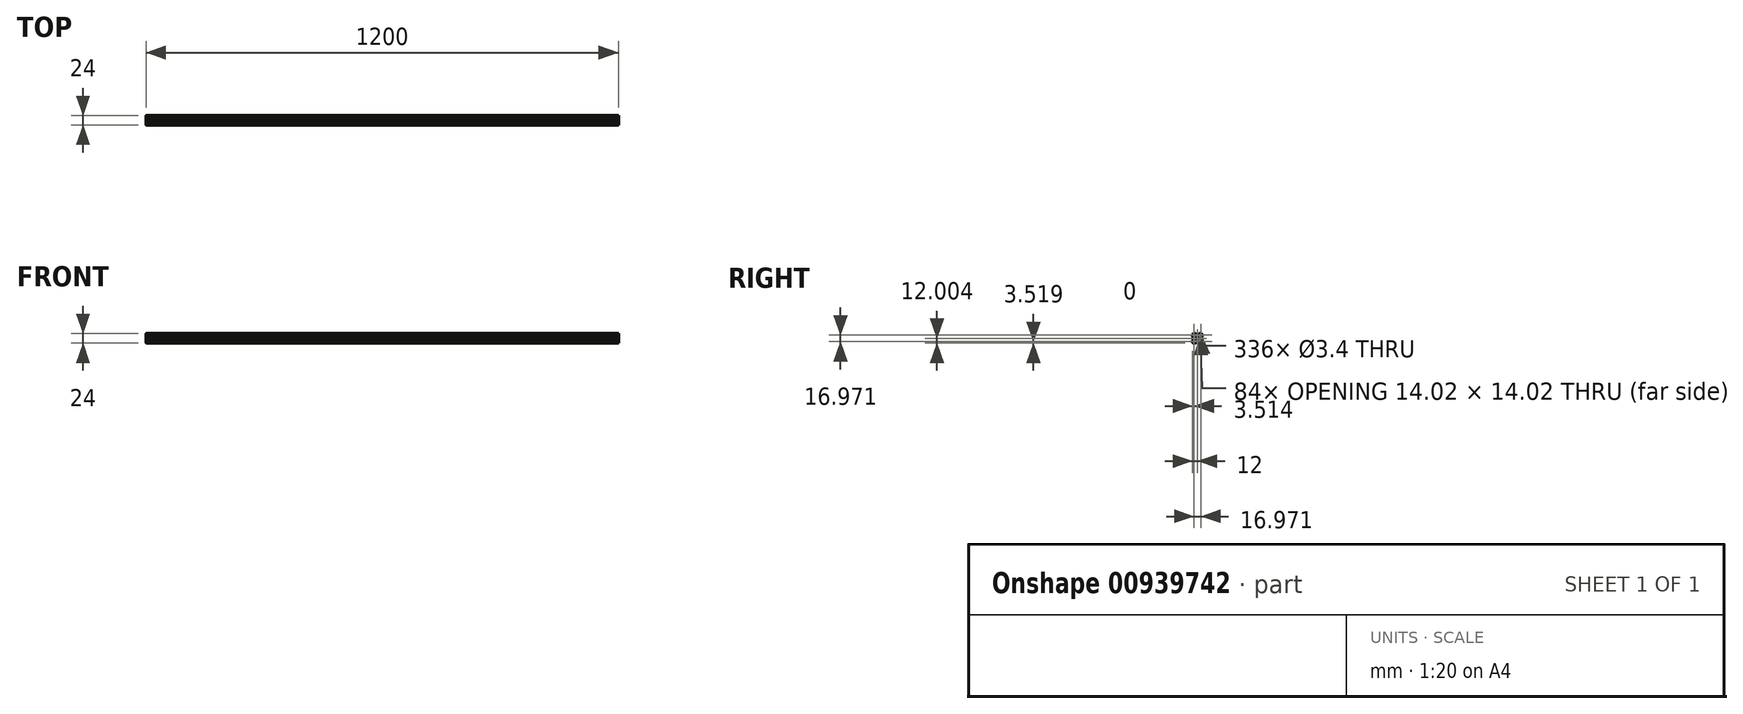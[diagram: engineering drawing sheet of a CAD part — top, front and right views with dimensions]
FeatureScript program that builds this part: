
annotation { "Feature Type Name" : "Feature", "Feature Type Description" : "" }
export const myFeature = defineFeature(function(context is Context, id is Id, definition is map)
    precondition{}
    {
        {
            var Q0;
            Q0=qCreatedBy(makeId("Right.planeOp"),FACE);
            var sketch = newSketch(context, id + "F0", { "sketchPlane" : qUnion([Q0])});
            skLineSegment(sketch, "E0.0.0", {"start": v(-5.44, -8.54) * mm, "end": v(5.56, -8.54) * mm});
            skLineSegment(sketch, "E0.0.1", {"start": v(5.56, -8.54) * mm, "end": v(5.56, -10.04) * mm});
            skLineSegment(sketch, "E0.0.2", {"start": v(5.56, -10.04) * mm, "end": v(4.06, -10.04) * mm});
            skLineSegment(sketch, "E0.0.3", {"start": v(4.06, -10.04) * mm, "end": v(4.06, -11.04) * mm});
            skLineSegment(sketch, "E0.0.4", {"start": v(4.06, -11.04) * mm, "end": v(5.06, -12.04) * mm});
            skLineSegment(sketch, "E0.0.5", {"start": v(5.06, -12.04) * mm, "end": v(8.04, -12.04) * mm});
            skLineSegment(sketch, "E0.0.6", {"start": v(8.04, -12.04) * mm, "end": v(8.54, -11.54) * mm});
            skLineSegment(sketch, "E0.0.7", {"start": v(8.54, -11.54) * mm, "end": v(9.04, -12.04) * mm});
            skLineSegment(sketch, "E0.0.8", {"start": v(9.04, -12.04) * mm, "end": v(10.57, -12.04) * mm});
            skArc(sketch, "E0.0.9", {"start": v(10.57, -12.04) * mm, "mid": v(11.34, -11.31) * mm, "end": v(12.06, -10.54) * mm});
            skLineSegment(sketch, "E0.0.10", {"start": v(12.06, -10.54) * mm, "end": v(12.06, -9.02) * mm});
            skLineSegment(sketch, "E0.0.11", {"start": v(12.06, -9.02) * mm, "end": v(11.56, -8.52) * mm});
            skLineSegment(sketch, "E0.0.12", {"start": v(11.56, -8.52) * mm, "end": v(12.06, -8.02) * mm});
            skLineSegment(sketch, "E0.0.13", {"start": v(12.06, -8.02) * mm, "end": v(12.06, -5.04) * mm});
            skLineSegment(sketch, "E0.0.14", {"start": v(12.06, -5.04) * mm, "end": v(11.06, -4.04) * mm});
            skLineSegment(sketch, "E0.0.15", {"start": v(11.06, -4.04) * mm, "end": v(10.06, -4.04) * mm});
            skLineSegment(sketch, "E0.0.16", {"start": v(10.06, -4.04) * mm, "end": v(10.06, -5.54) * mm});
            skLineSegment(sketch, "E0.0.17", {"start": v(10.06, -5.54) * mm, "end": v(8.56, -5.54) * mm});
            skLineSegment(sketch, "E0.0.18", {"start": v(8.56, -5.54) * mm, "end": v(8.56, 5.46) * mm});
            skLineSegment(sketch, "E0.0.19", {"start": v(8.56, 5.46) * mm, "end": v(10.06, 5.46) * mm});
            skLineSegment(sketch, "E0.0.20", {"start": v(10.06, 5.46) * mm, "end": v(10.06, 3.96) * mm});
            skLineSegment(sketch, "E0.0.21", {"start": v(10.06, 3.96) * mm, "end": v(11.06, 3.96) * mm});
            skLineSegment(sketch, "E0.0.22", {"start": v(11.06, 3.96) * mm, "end": v(12.06, 4.96) * mm});
            skLineSegment(sketch, "E0.0.23", {"start": v(12.06, 4.96) * mm, "end": v(12.06, 7.95) * mm});
            skLineSegment(sketch, "E0.0.24", {"start": v(12.06, 7.95) * mm, "end": v(11.56, 8.45) * mm});
            skLineSegment(sketch, "E0.0.25", {"start": v(11.56, 8.45) * mm, "end": v(12.06, 8.95) * mm});
            skLineSegment(sketch, "E0.0.26", {"start": v(12.06, 8.95) * mm, "end": v(12.06, 10.47) * mm});
            skArc(sketch, "E0.0.27", {"start": v(12.06, 10.47) * mm, "mid": v(11.34, 11.24) * mm, "end": v(10.57, 11.96) * mm});
            skLineSegment(sketch, "E0.0.28", {"start": v(10.57, 11.96) * mm, "end": v(9.04, 11.96) * mm});
            skLineSegment(sketch, "E0.0.29", {"start": v(9.04, 11.96) * mm, "end": v(8.54, 11.46) * mm});
            skLineSegment(sketch, "E0.0.30", {"start": v(8.54, 11.46) * mm, "end": v(8.04, 11.96) * mm});
            skLineSegment(sketch, "E0.0.31", {"start": v(8.04, 11.96) * mm, "end": v(5.06, 11.96) * mm});
            skLineSegment(sketch, "E0.0.32", {"start": v(5.06, 11.96) * mm, "end": v(4.06, 10.96) * mm});
            skLineSegment(sketch, "E0.0.33", {"start": v(4.06, 10.96) * mm, "end": v(4.06, 9.96) * mm});
            skLineSegment(sketch, "E0.0.34", {"start": v(4.06, 9.96) * mm, "end": v(5.56, 9.96) * mm});
            skLineSegment(sketch, "E0.0.35", {"start": v(5.56, 9.96) * mm, "end": v(5.56, 8.46) * mm});
            skLineSegment(sketch, "E0.0.36", {"start": v(5.56, 8.46) * mm, "end": v(-5.44, 8.46) * mm});
            skLineSegment(sketch, "E0.0.37", {"start": v(-5.44, 8.46) * mm, "end": v(-5.44, 9.96) * mm});
            skLineSegment(sketch, "E0.0.38", {"start": v(-5.44, 9.96) * mm, "end": v(-3.94, 9.96) * mm});
            skLineSegment(sketch, "E0.0.39", {"start": v(-3.94, 9.96) * mm, "end": v(-3.94, 10.96) * mm});
            skLineSegment(sketch, "E0.0.40", {"start": v(-3.94, 10.96) * mm, "end": v(-4.94, 11.96) * mm});
            skLineSegment(sketch, "E0.0.41", {"start": v(-4.94, 11.96) * mm, "end": v(-7.93, 11.96) * mm});
            skLineSegment(sketch, "E0.0.42", {"start": v(-7.93, 11.96) * mm, "end": v(-8.43, 11.46) * mm});
            skLineSegment(sketch, "E0.0.43", {"start": v(-8.43, 11.46) * mm, "end": v(-8.93, 11.96) * mm});
            skLineSegment(sketch, "E0.0.44", {"start": v(-8.93, 11.96) * mm, "end": v(-10.45, 11.96) * mm});
            skArc(sketch, "E0.0.45", {"start": v(-10.45, 11.96) * mm, "mid": v(-11.22, 11.24) * mm, "end": v(-11.94, 10.47) * mm});
            skLineSegment(sketch, "E0.0.46", {"start": v(-11.94, 10.47) * mm, "end": v(-11.94, 8.95) * mm});
            skLineSegment(sketch, "E0.0.47", {"start": v(-11.94, 8.95) * mm, "end": v(-11.44, 8.45) * mm});
            skLineSegment(sketch, "E0.0.48", {"start": v(-11.44, 8.45) * mm, "end": v(-11.94, 7.95) * mm});
            skLineSegment(sketch, "E0.0.49", {"start": v(-11.94, 7.95) * mm, "end": v(-11.94, 4.96) * mm});
            skLineSegment(sketch, "E0.0.50", {"start": v(-11.94, 4.96) * mm, "end": v(-10.94, 3.96) * mm});
            skLineSegment(sketch, "E0.0.51", {"start": v(-10.94, 3.96) * mm, "end": v(-9.94, 3.96) * mm});
            skLineSegment(sketch, "E0.0.52", {"start": v(-9.94, 3.96) * mm, "end": v(-9.94, 5.46) * mm});
            skLineSegment(sketch, "E0.0.53", {"start": v(-9.94, 5.46) * mm, "end": v(-8.44, 5.46) * mm});
            skLineSegment(sketch, "E0.0.54", {"start": v(-8.44, 5.46) * mm, "end": v(-8.44, -5.54) * mm});
            skLineSegment(sketch, "E0.0.55", {"start": v(-8.44, -5.54) * mm, "end": v(-9.94, -5.54) * mm});
            skLineSegment(sketch, "E0.0.56", {"start": v(-9.94, -5.54) * mm, "end": v(-9.94, -4.04) * mm});
            skLineSegment(sketch, "E0.0.57", {"start": v(-9.94, -4.04) * mm, "end": v(-10.94, -4.04) * mm});
            skLineSegment(sketch, "E0.0.58", {"start": v(-10.94, -4.04) * mm, "end": v(-11.94, -5.04) * mm});
            skLineSegment(sketch, "E0.0.59", {"start": v(-11.94, -5.04) * mm, "end": v(-11.94, -8.02) * mm});
            skLineSegment(sketch, "E0.0.60", {"start": v(-11.94, -8.02) * mm, "end": v(-11.44, -8.52) * mm});
            skLineSegment(sketch, "E0.0.61", {"start": v(-11.44, -8.52) * mm, "end": v(-11.94, -9.02) * mm});
            skLineSegment(sketch, "E0.0.62", {"start": v(-11.94, -9.02) * mm, "end": v(-11.94, -10.54) * mm});
            skArc(sketch, "E0.0.63", {"start": v(-11.94, -10.54) * mm, "mid": v(-11.22, -11.31) * mm, "end": v(-10.45, -12.04) * mm});
            skLineSegment(sketch, "E0.0.64", {"start": v(-10.45, -12.04) * mm, "end": v(-8.93, -12.04) * mm});
            skLineSegment(sketch, "E0.0.65", {"start": v(-8.93, -12.04) * mm, "end": v(-8.43, -11.54) * mm});
            skLineSegment(sketch, "E0.0.66", {"start": v(-8.43, -11.54) * mm, "end": v(-7.93, -12.04) * mm});
            skLineSegment(sketch, "E0.0.67", {"start": v(-7.93, -12.04) * mm, "end": v(-4.94, -12.04) * mm});
            skLineSegment(sketch, "E0.0.68", {"start": v(-4.94, -12.04) * mm, "end": v(-3.94, -11.04) * mm});
            skLineSegment(sketch, "E0.0.69", {"start": v(-3.94, -11.04) * mm, "end": v(-3.94, -10.04) * mm});
            skLineSegment(sketch, "E0.0.70", {"start": v(-3.94, -10.04) * mm, "end": v(-5.44, -10.04) * mm});
            skLineSegment(sketch, "E0.0.71", {"start": v(-5.44, -10.04) * mm, "end": v(-5.44, -8.54) * mm});
            skCircle(sketch, "E1.0", {"center": v(8.54, -8.52) * mm, "radius": 1.7 * mm});
            skCircle(sketch, "E2.0", {"center": v(-8.43, -8.52) * mm, "radius": 1.7 * mm});
            skArc(sketch, "E3.0", {"start": v(3.57, -6.1) * mm, "mid": v(0.06, -7.05) * mm, "end": v(-3.45, -6.1) * mm});
            skLineSegment(sketch, "E4.0", {"start": v(-3.7, -6.04) * mm, "end": v(-5.44, -6.04) * mm});
            skArc(sketch, "E5.0", {"start": v(-3.45, -6.1) * mm, "mid": v(-3.57, -6.05) * mm, "end": v(-3.7, -6.04) * mm});
            skArc(sketch, "E6.0", {"start": v(-5.44, -6.04) * mm, "mid": v(-5.8, -5.89) * mm, "end": v(-5.94, -5.54) * mm});
            skLineSegment(sketch, "E7.0", {"start": v(-5.94, -3.8) * mm, "end": v(-5.94, -5.54) * mm});
            skArc(sketch, "E8.0", {"start": v(-6, -3.55) * mm, "mid": v(-6.95, -0.04) * mm, "end": v(-6, 3.48) * mm});
            skArc(sketch, "E9.0", {"start": v(-5.94, -3.8) * mm, "mid": v(-5.96, -3.67) * mm, "end": v(-6, -3.55) * mm});
            skLineSegment(sketch, "E10.0", {"start": v(-5.94, 5.46) * mm, "end": v(-5.94, 3.73) * mm});
            skPoint(sketch, "E11.0", {"position": v(-5.96, 3.6) * mm});
            skArc(sketch, "E12.0", {"start": v(-5.94, 5.46) * mm, "mid": v(-5.8, 5.82) * mm, "end": v(-5.44, 5.96) * mm});
            skLineSegment(sketch, "E13.0", {"start": v(-3.7, 5.96) * mm, "end": v(-5.44, 5.96) * mm});
            skArc(sketch, "E14.0", {"start": v(-3.45, 6.03) * mm, "mid": v(0.06, 6.97) * mm, "end": v(3.57, 6.03) * mm});
            skArc(sketch, "E15.0", {"start": v(-3.7, 5.96) * mm, "mid": v(-3.57, 5.98) * mm, "end": v(-3.45, 6.03) * mm});
            skLineSegment(sketch, "E16.0", {"start": v(5.56, 5.96) * mm, "end": v(3.82, 5.96) * mm});
            skArc(sketch, "E17.0", {"start": v(3.57, 6.03) * mm, "mid": v(3.7, 5.98) * mm, "end": v(3.82, 5.96) * mm});
            skArc(sketch, "E18.0", {"start": v(5.56, 5.96) * mm, "mid": v(5.91, 5.82) * mm, "end": v(6.06, 5.46) * mm});
            skLineSegment(sketch, "E19.0", {"start": v(6.06, 5.46) * mm, "end": v(6.06, 3.73) * mm});
            skArc(sketch, "E20.0", {"start": v(6.13, 3.48) * mm, "mid": v(7.07, -0.04) * mm, "end": v(6.13, -3.55) * mm});
            skArc(sketch, "E21.0", {"start": v(6.06, 3.73) * mm, "mid": v(6.08, 3.6) * mm, "end": v(6.13, 3.48) * mm});
            skCircle(sketch, "E22.0", {"center": v(-8.43, 8.45) * mm, "radius": 1.7 * mm});
            skCircle(sketch, "E23.0", {"center": v(8.54, 8.45) * mm, "radius": 1.7 * mm});
            skLineSegment(sketch, "E24.0", {"start": v(5.56, -6.04) * mm, "end": v(3.82, -6.04) * mm});
            skArc(sketch, "E25.0", {"start": v(6.06, -5.54) * mm, "mid": v(5.91, -5.89) * mm, "end": v(5.56, -6.04) * mm});
            skLineSegment(sketch, "E26.0", {"start": v(6.06, -3.8) * mm, "end": v(6.06, -5.54) * mm});
            skArc(sketch, "E27.0", {"start": v(3.82, -6.04) * mm, "mid": v(3.7, -6.05) * mm, "end": v(3.57, -6.1) * mm});
            skArc(sketch, "E28.0", {"start": v(6.13, -3.55) * mm, "mid": v(6.08, -3.67) * mm, "end": v(6.06, -3.8) * mm});
            skArc(sketch, "E29.0", {"start": v(-6, 3.48) * mm, "mid": v(-5.96, 3.6) * mm, "end": v(-5.94, 3.73) * mm});
            skSolve(sketch);
        }
        {
            var Q0;
            Q0=qSketchRegion(id+"F0",true);
            extrude(context, id + "F1", {"entities" : qUnion([Q0]), "depth" : 48 * mm, "offsetDistance" : 25 * mm});
        }
        {
            var Q0;
            Q0=qSketchRegion(id+"F0",true);
            extrude(context, id + "F2", {"entities" : qUnion([Q0]), "depth" : 72 * mm, "offsetDistance" : 25 * mm});
        }
        {
            var Q0;
            Q0=qSketchRegion(id+"F0",true);
            extrude(context, id + "F3", {"entities" : qUnion([Q0]), "depth" : 96 * mm, "offsetDistance" : 25 * mm});
        }
        {
            var Q0;
            Q0=qSketchRegion(id+"F0",true);
            extrude(context, id + "F4", {"entities" : qUnion([Q0]), "depth" : 120 * mm, "offsetDistance" : 25 * mm});
        }
        {
            var Q0;
            Q0=qSketchRegion(id+"F0",true);
            extrude(context, id + "F5", {"entities" : qUnion([Q0]), "depth" : 144 * mm, "offsetDistance" : 25 * mm});
        }
        {
            var Q0;
            Q0=qSketchRegion(id+"F0",true);
            extrude(context, id + "F6", {"entities" : qUnion([Q0]), "depth" : 192 * mm, "offsetDistance" : 25 * mm});
        }
        {
            var Q0;
            Q0=qSketchRegion(id+"F0",true);
            extrude(context, id + "F7", {"entities" : qUnion([Q0]), "depth" : 288 * mm, "offsetDistance" : 25 * mm});
        }
        {
            var Q0;
            Q0=qSketchRegion(id+"F0",true);
            extrude(context, id + "F8", {"entities" : qUnion([Q0]), "depth" : 336 * mm, "offsetDistance" : 25 * mm});
        }
        {
            var Q0;
            Q0=qSketchRegion(id+"F0",true);
            extrude(context, id + "F9", {"entities" : qUnion([Q0]), "depth" : 384 * mm, "offsetDistance" : 25 * mm});
        }
        {
            var Q0;
            Q0=qSketchRegion(id+"F0",true);
            extrude(context, id + "F10", {"entities" : qUnion([Q0]), "depth" : 432 * mm, "offsetDistance" : 25 * mm});
        }
        {
            var Q0;
            Q0=qSketchRegion(id+"F0",true);
            extrude(context, id + "F11", {"entities" : qUnion([Q0]), "depth" : 528 * mm, "offsetDistance" : 25 * mm});
        }
        {
            var Q0;
            Q0=qSketchRegion(id+"F0",true);
            extrude(context, id + "F12", {"entities" : qUnion([Q0]), "depth" : 624 * mm, "offsetDistance" : 25 * mm});
        }
        {
            var Q0;
            Q0=qSketchRegion(id+"F0",true);
            extrude(context, id + "F13", {"entities" : qUnion([Q0]), "depth" : 912 * mm, "offsetDistance" : 25 * mm});
        }
        {
            var Q0;
            Q0=qSketchRegion(id+"F0",true);
            extrude(context, id + "F14", {"entities" : qUnion([Q0]), "depth" : 1200 * mm, "offsetDistance" : 25 * mm});
        }
    });
